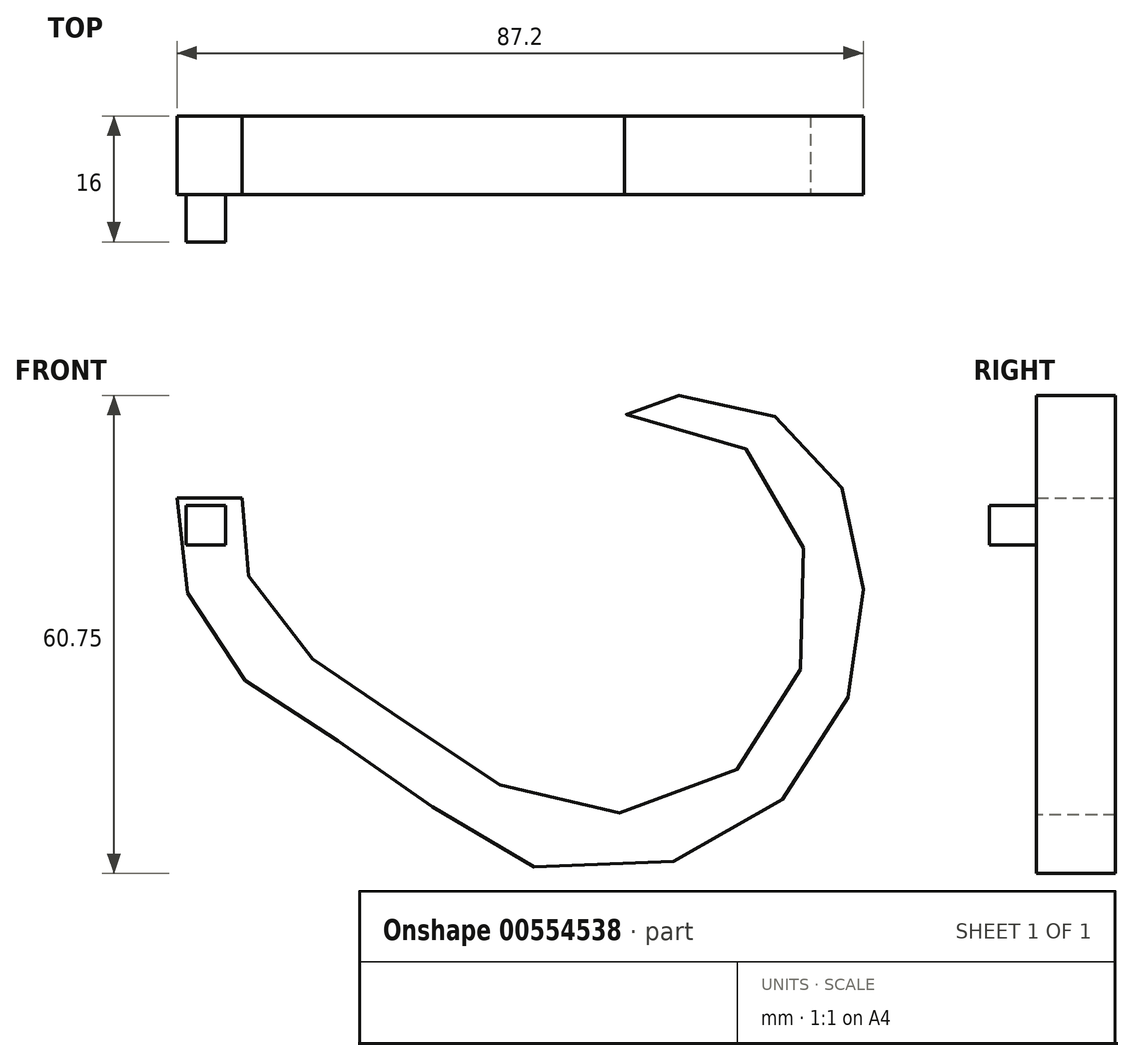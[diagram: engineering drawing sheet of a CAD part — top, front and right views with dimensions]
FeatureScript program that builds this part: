
annotation { "Feature Type Name" : "Feature", "Feature Type Description" : "" }
export const myFeature = defineFeature(function(context is Context, id is Id, definition is map)
    precondition{}
    {
        {
            var Q0;
            Q0=qCreatedBy(makeId("Front.planeOp"),FACE);
            var sketch = newSketch(context, id + "F0", { "sketchPlane" : qUnion([Q0])});
            skLineSegment(sketch, "E0", {"start": v(-43.88, 27.1) * mm, "end": v(-35.58, 27.1) * mm});
            skFitSpline(sketch, "E1", {"points": [v(-35.58, 27.1) * mm, v(-35.58, 22) * mm, v(-33.88, 14.97) * mm, v(-26.64, 6.68) * mm, v(-17.07, 0) * mm, v(-6.85, -6.52) * mm, v(4.42, -12.69) * mm, v(21.23, -10.77) * mm, v(30.8, -3.75) * mm, v(36.34, 9.87) * mm, v(35.06, 23.27) * mm, v(28.04, 33.48) * mm, v(13.36, 37.53) * mm, v(13.41, 39.22) * mm, v(17.43, 40.1) * mm, v(25.27, 39.6) * mm, v(34.38, 36.18) * mm, v(40.2, 29.22) * mm, v(43.1, 18.34) * mm, v(43.04, 10.81) * mm, v(39.43, -3.48) * mm, v(30.4, -13.26) * mm, v(16.26, -19.88) * mm, v(-1.65, -18.83) * mm, v(-12.03, -11.6) * mm, v(-22.4, -4.38) * mm, v(-32.34, 1.48) * mm, v(-40.2, 9.98) * mm, v(-43.35, 18.4) * mm, v(-43.88, 27.1) * mm], "startDerivative": vector(-7.27, -207.9) * mm, "endDerivative": vector(-2.2, 278.65) * mm});
            skPoint(sketch, "E2.middle", {"position": v(-39.83, 23.6) * mm});
            skSolve(sketch);
        }
        {
            var Q0;
            Q0=makeQuery(id+"F0.imprint","IMPRINT",FACE,{"disambiguationData":[TD([[makeQuery(id+"F0.imprint","IMPRINT",EDGE,{"derivedFrom":sQuery(id+"F0.wireOp",EDGE,"E0")}),-1.0]])]});
            extrude(context, id + "F1", {"entities" : qUnion([Q0]), "depth" : 10 * mm, "offsetDistance" : 25 * mm});
        }
        {
            var Q0;
            Q0=makeQuery(id+"F1.opExtrude","CAP_FACE",FACE,{"disambiguationData":[OSD([sQuery(id+"F0.wireOp",EDGE,"E0"),sQuery(id+"F0.wireOp",EDGE,"E1")])],"isStart":false});
            var sketch = newSketch(context, id + "F2", { "sketchPlane" : qUnion([Q0])});
            skLineSegment(sketch, "E3.bottom", {"start": v(-37.73, 26.1) * mm, "end": v(-42.73, 26.1) * mm});
            skLineSegment(sketch, "E3.top", {"start": v(-37.73, 21.1) * mm, "end": v(-42.73, 21.1) * mm});
            skLineSegment(sketch, "E3.left", {"start": v(-37.73, 26.1) * mm, "end": v(-37.73, 21.1) * mm});
            skLineSegment(sketch, "E3.right", {"start": v(-42.73, 26.1) * mm, "end": v(-42.73, 21.1) * mm});
            skPoint(sketch, "E3.middle", {"position": v(-40.23, 23.6) * mm});
            skSolve(sketch);
        }
        {
            var Q0;
            Q0=makeQuery(id+"F2.imprint","IMPRINT",FACE,{"disambiguationData":[TD([[makeQuery(id+"F2.imprint","IMPRINT",EDGE,{"derivedFrom":sQuery(id+"F2.wireOp",EDGE,"E3.bottom")}),1.0]])]});
            extrude(context, id + "F3", {"entities" : qUnion([Q0]), "operationType" : NewBodyOperationType.ADD, "depth" : 6 * mm, "offsetDistance" : 25 * mm});
        }
    });
